# Revit family: Legrand Export Ovaline Column Kit
name_source: partatom
category: Installations électriques
units: mm (PartAtom-declared; Revit-internal decimal feet)

## family parameters
Conserver l'orientation des annotations = Non
Cote de connecteur circulaire = Utiliser le diamètre
Couper avec des vides une fois chargée = Non
Hôte = Face
Partagée = Non
Point de calcul de pièce = Non
Type d'élément = Normal

## types (6) — shared parameters
Fabricant = LEGRAND
Main Material = Aluminum
Number of compartments = Other
Standard = Ovaline
h1 = 2700 mm  [stored 8.85827 ft]
zero-valued in all types: Elévation par défaut

## per-type parameters (varying)
| type | Description | Finishing | Modèle |
| Ovaline kit mini Column 1C White | ovaline kit extension for mini Column 1 cpt cv45mm White | White | LG-653060 |
| Ovaline kit mini Column 1C Alu | ovaline kit extension for mini Column 1 cpt cv45mm Alu | Aluminum | LG-653061 |
| Ovaline kit mini  Column 1C Black | ovaline kit extension for mini Column 1 cpt cv45mm Black | Black | LG-653062 |
| Ovaline kit mini Column T2 White | ovaline kit extension for mini Column 2 cpts cv45mm or 1 cpt cv80mm White | White | LG-653063 |
| Ovaline kit mini Column T2 Alu | ovaline kit extension for mini Column 2 cpts cv45mm or 1 cpt cv80mm Alu | Aluminum | LG-653064 |
| Ovaline kit mini Column T2 Black | ovaline kit extension for mini Column 2 cpts cv45mm or 1 cpt cv80mm Black | Black | LG-653065 |

note: [stored X ft] marks values corroborated as IEEE doubles in the binary element streams (Revit-internal decimal feet)
